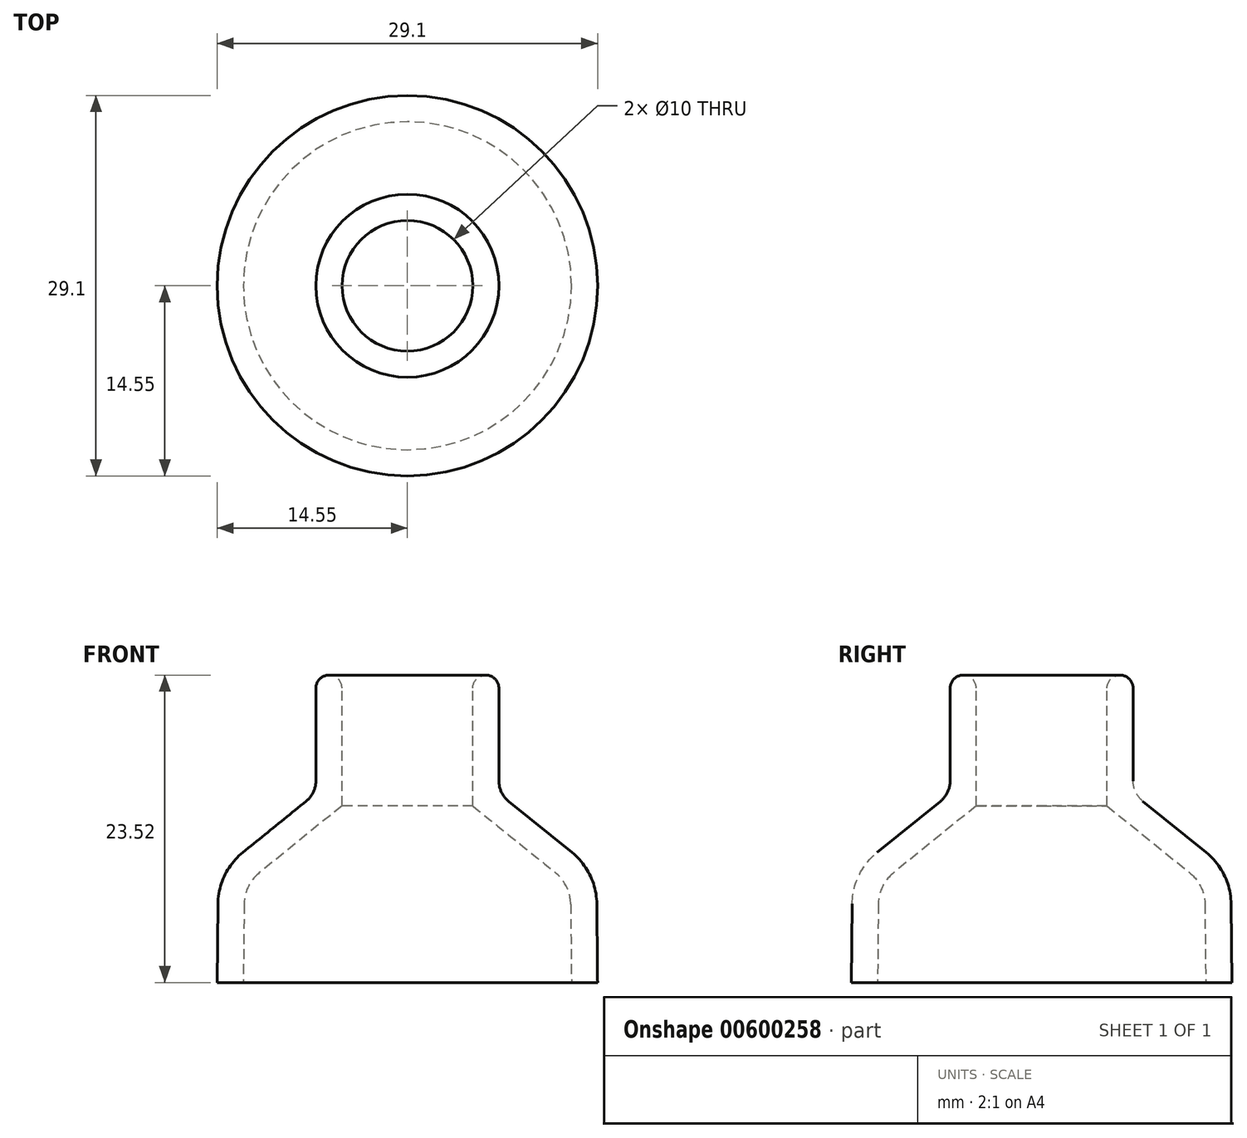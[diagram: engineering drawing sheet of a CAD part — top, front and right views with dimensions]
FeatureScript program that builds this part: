
annotation { "Feature Type Name" : "Feature", "Feature Type Description" : "" }
export const myFeature = defineFeature(function(context is Context, id is Id, definition is map)
    precondition{}
    {
        {
            var Q0;
            Q0=qCreatedBy(makeId("Front.planeOp"),FACE);
            var sketch = newSketch(context, id + "F0", { "sketchPlane" : qUnion([Q0])});
            skLineSegment(sketch, "E0", {"start": v(0, 0) * mm, "end": v(12.55, 0) * mm, "construction": true});
            skLineSegment(sketch, "E1", {"start": v(0, 6) * mm, "end": v(12.5, 6) * mm, "construction": true});
            skLineSegment(sketch, "E2", {"start": v(0, 0) * mm, "end": v(0, 6) * mm, "construction": true});
            skLineSegment(sketch, "E3", {"start": v(12.55, 0) * mm, "end": v(12.5, 6) * mm});
            skArc(sketch, "E4", {"start": v(12.5, 6) * mm, "mid": v(12.18, 7.33) * mm, "end": v(11.33, 8.4) * mm});
            skPoint(sketch, "E4.second.point", {"position": v(6.25, 6) * mm});
            skPoint(sketch, "E4.third.point", {"position": v(12.5, 6) * mm});
            skLineSegment(sketch, "E5", {"start": v(5, 13.52) * mm, "end": v(5, 21.52) * mm});
            skLineSegment(sketch, "E6", {"start": v(5, 21.52) * mm, "end": v(0, 21.52) * mm});
            skLineSegment(sketch, "E7", {"start": v(0, 21.52) * mm, "end": v(0, 0) * mm});
            skLineSegment(sketch, "E8", {"start": v(0, 0) * mm, "end": v(12.55, 0) * mm});
            skLineSegment(sketch, "E9", {"start": v(11.33, 8.4) * mm, "end": v(5, 13.52) * mm});
            skSolve(sketch);
        }
        {
            var Q0;
            Q0=makeQuery(id+"F0.imprint","IMPRINT",FACE,{"disambiguationData":[TD([[makeQuery(id+"F0.imprint","IMPRINT",EDGE,{"derivedFrom":sQuery(id+"F0.wireOp",EDGE,"E3")}),1.0]])]});
            var Q1;
            Q1=sQuery(id+"F0.wireOp",EDGE,"E7");
            revolve(context, id + "F1", {"entities" : qUnion([Q0]), "axis" : qUnion([Q1]), "revolveType" : RevolveType.FULL});
        }
        {
            var Q0;
            Q0=makeQuery(id+"F1.opRevolve","SWEPT_FACE",FACE,{"disambiguationData":[OSD([sQuery(id+"F0.wireOp",EDGE,"E8")])]});
            shell(context, id + "F2", {"entities" : qUnion([Q0]), "thickness" : 2 * mm, "oppositeDirection" : true});
        }
        {
            var Q0;
            Q0=makeQuery(id+"F2.opShell","OFFSET_FACE",FACE,{"disambiguationData":[OSD([sQuery(id+"F0.wireOp",EDGE,"E6")])]});
            extrude(context, id + "F3", {"entities" : qUnion([Q0]), "operationType" : NewBodyOperationType.REMOVE, "endBound" : BoundingType.THROUGH_ALL, "oppositeDirection" : true, "depth" : 25 * mm, "offsetDistance" : 25 * mm});
        }
        {
            var Q0;
            Q0=makeQuery(id+"F1.opRevolve","SWEPT_EDGE",EDGE,{"disambiguationData":[OSD([sQuery(id+"F0.wireOp",EDGE,"E5"),sQuery(id+"F0.wireOp",EDGE,"E6")])]});
            var Q1;
            {var subQ0=sQuery(id+"F0.wireOp",EDGE,"E6");Q1=makeQuery(id+"F3.boolean.opBoolean","INTERSECT",EDGE,{"derivedFrom":[makeQuery(id+"F1.opRevolve","SWEPT_FACE",FACE,{"disambiguationData":[OSD([subQ0])]}),makeQuery(id+"F3.opExtrude","SWEPT_FACE",FACE,{"disambiguationData":[OSD([sQuery(id+"F0.wireOp",EDGE,"E5"),subQ0])]})]});}
            fillet(context, id + "F4", {"entities" : qUnion([Q0, Q1]), "radius" : 1 * mm, "tangentPropagation" : true, "allowEdgeOverflow" : false});
        }
        {
            var Q0;
            Q0=makeQuery(id+"F1.opRevolve","SWEPT_EDGE",EDGE,{"disambiguationData":[OSD([sQuery(id+"F0.wireOp",EDGE,"E5"),sQuery(id+"F0.wireOp",EDGE,"E9")])]});
            fillet(context, id + "F5", {"entities" : qUnion([Q0]), "radius" : 2 * mm, "tangentPropagation" : true, "allowEdgeOverflow" : false});
        }
    });
